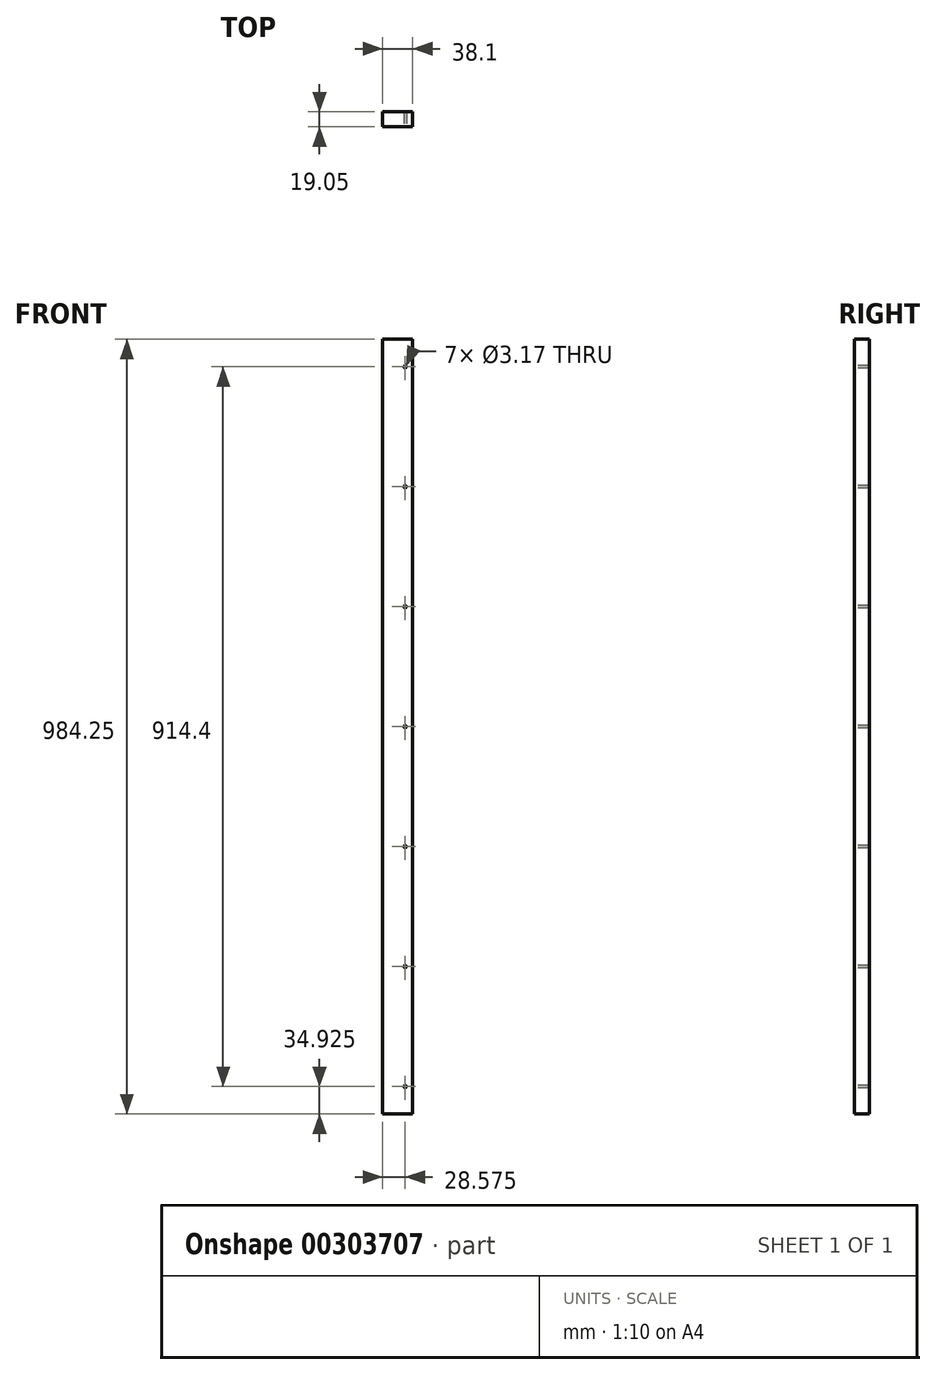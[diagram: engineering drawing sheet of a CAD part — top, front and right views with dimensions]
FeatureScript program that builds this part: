
annotation { "Feature Type Name" : "Feature", "Feature Type Description" : "" }
export const myFeature = defineFeature(function(context is Context, id is Id, definition is map)
    precondition{}
    {
        {
            var Q0;
            Q0=qCreatedBy(makeId("Front.planeOp"),FACE);
            var sketch = newSketch(context, id + "F0", { "sketchPlane" : qUnion([Q0])});
            skLineSegment(sketch, "E0.bottom", {"start": v(0, 0) * mm, "end": v(38.1, 0) * mm});
            skLineSegment(sketch, "E0.top", {"start": v(0, -984.25) * mm, "end": v(38.1, -984.25) * mm});
            skLineSegment(sketch, "E0.left", {"start": v(0, 0) * mm, "end": v(0, -984.25) * mm});
            skLineSegment(sketch, "E0.right", {"start": v(38.1, 0) * mm, "end": v(38.1, -984.25) * mm});
            skSolve(sketch);
        }
        {
            var Q0;
            Q0=qSketchRegion(id+"F0",true);
            extrude(context, id + "F1", {"entities" : qUnion([Q0]), "oppositeDirection" : true, "depth" : 19.05 * mm});
        }
        {
            var Q0;
            Q0=qCreatedBy(makeId("Front.planeOp"),FACE);
            var sketch = newSketch(context, id + "F2", { "sketchPlane" : qUnion([Q0])});
            skCircle(sketch, "E1", {"center": v(28.57, -34.92) * mm, "radius": 1.59 * mm});
            skCircle(sketch, "E2.1.0.0", {"center": v(28.57, -187.32) * mm, "radius": 1.59 * mm});
            skCircle(sketch, "E2.2.0.0", {"center": v(28.57, -339.72) * mm, "radius": 1.59 * mm});
            skCircle(sketch, "E2.3.0.0", {"center": v(28.57, -492.12) * mm, "radius": 1.59 * mm});
            skCircle(sketch, "E2.4.0.0", {"center": v(28.57, -644.52) * mm, "radius": 1.59 * mm});
            skCircle(sketch, "E2.5.0.0", {"center": v(28.57, -796.92) * mm, "radius": 1.59 * mm});
            skLineSegment(sketch, "E2.direction1", {"start": v(28.57, -34.92) * mm, "end": v(28.57, -187.32) * mm, "construction": true});
            skCircle(sketch, "E3.0.6.0", {"center": v(28.57, -949.32) * mm, "radius": 1.59 * mm});
            skSolve(sketch);
        }
        {
            var Q0;
            Q0=qSketchRegion(id+"F2",true);
            extrude(context, id + "F3", {"entities" : qUnion([Q0]), "operationType" : NewBodyOperationType.REMOVE, "endBound" : BoundingType.THROUGH_ALL, "oppositeDirection" : true, "depth" : 25.4 * mm});
        }
    });
